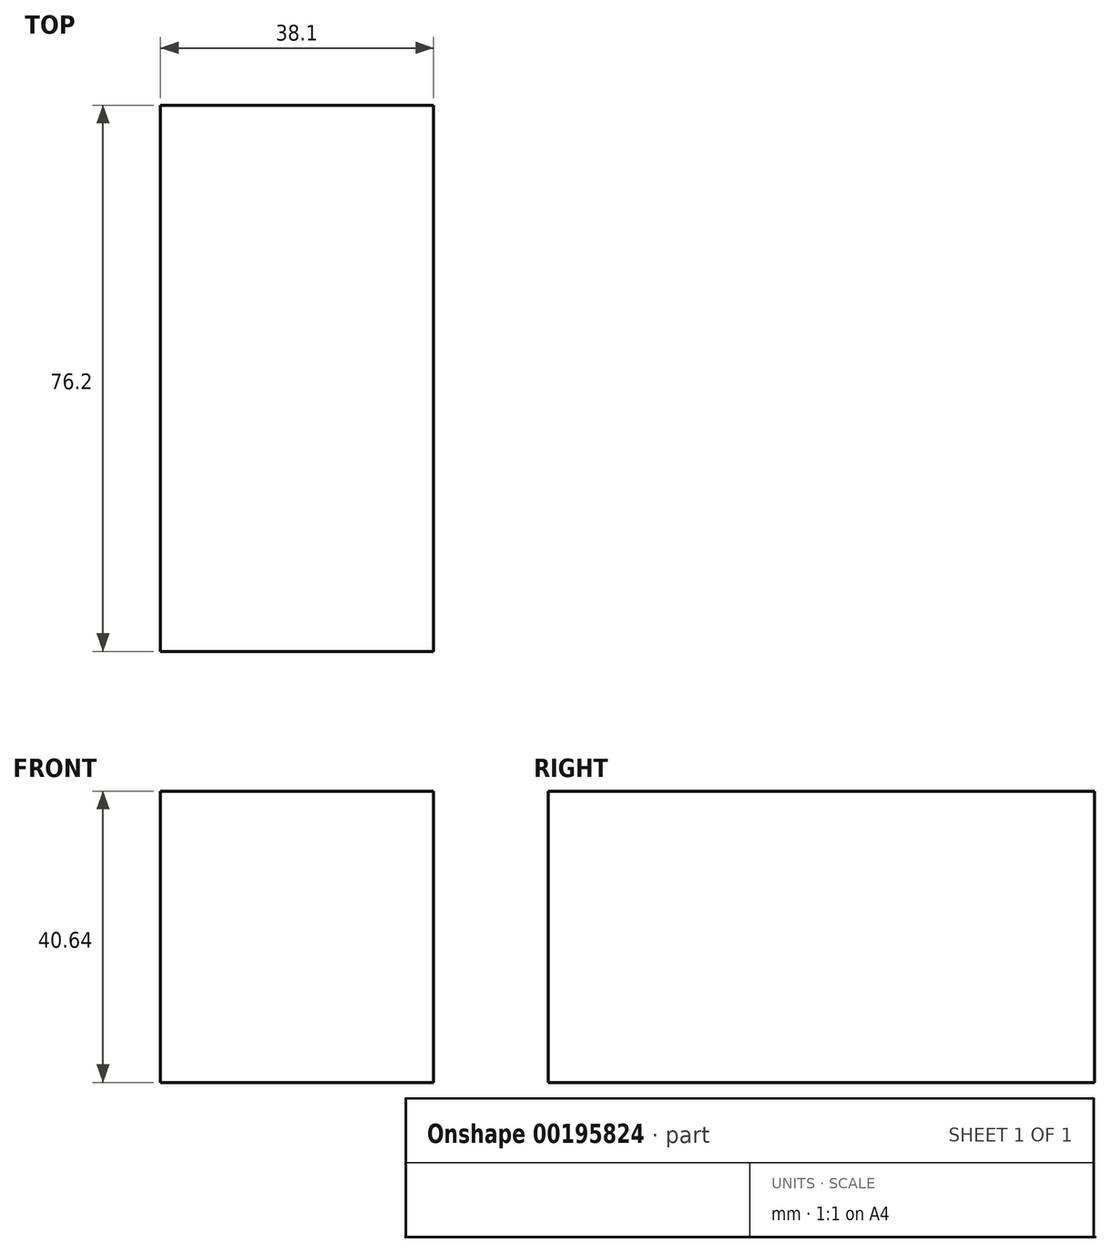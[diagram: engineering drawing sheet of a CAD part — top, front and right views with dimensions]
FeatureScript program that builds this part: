
annotation { "Feature Type Name" : "Feature", "Feature Type Description" : "" }
export const myFeature = defineFeature(function(context is Context, id is Id, definition is map)
    precondition{}
    {
        {
            var Q0;
            Q0=qCreatedBy(makeId("Top.planeOp"),FACE);
            var sketch = newSketch(context, id + "F0", { "sketchPlane" : qUnion([Q0])});
            skLineSegment(sketch, "E0.bottom", {"start": v(-38.86, 38.1) * mm, "end": v(-0.76, 38.1) * mm});
            skLineSegment(sketch, "E0.top", {"start": v(-38.86, -38.1) * mm, "end": v(-0.76, -38.1) * mm});
            skLineSegment(sketch, "E0.left", {"start": v(-38.86, 38.1) * mm, "end": v(-38.86, -38.1) * mm});
            skLineSegment(sketch, "E0.right", {"start": v(-0.76, 38.1) * mm, "end": v(-0.76, -38.1) * mm});
            skPoint(sketch, "E0.middle", {"position": v(-19.8, 0) * mm});
            skSolve(sketch);
        }
        {
            var Q0;
            Q0=makeQuery(id+"F0.imprint","IMPRINT",FACE,{"disambiguationData":[TD([[makeQuery(id+"F0.imprint","IMPRINT",EDGE,{"derivedFrom":sQuery(id+"F0.wireOp",EDGE,"E0.bottom")}),-1.0]])]});
            extrude(context, id + "F1", {"entities" : qUnion([Q0]), "depth" : 40.64 * mm});
        }
    });
